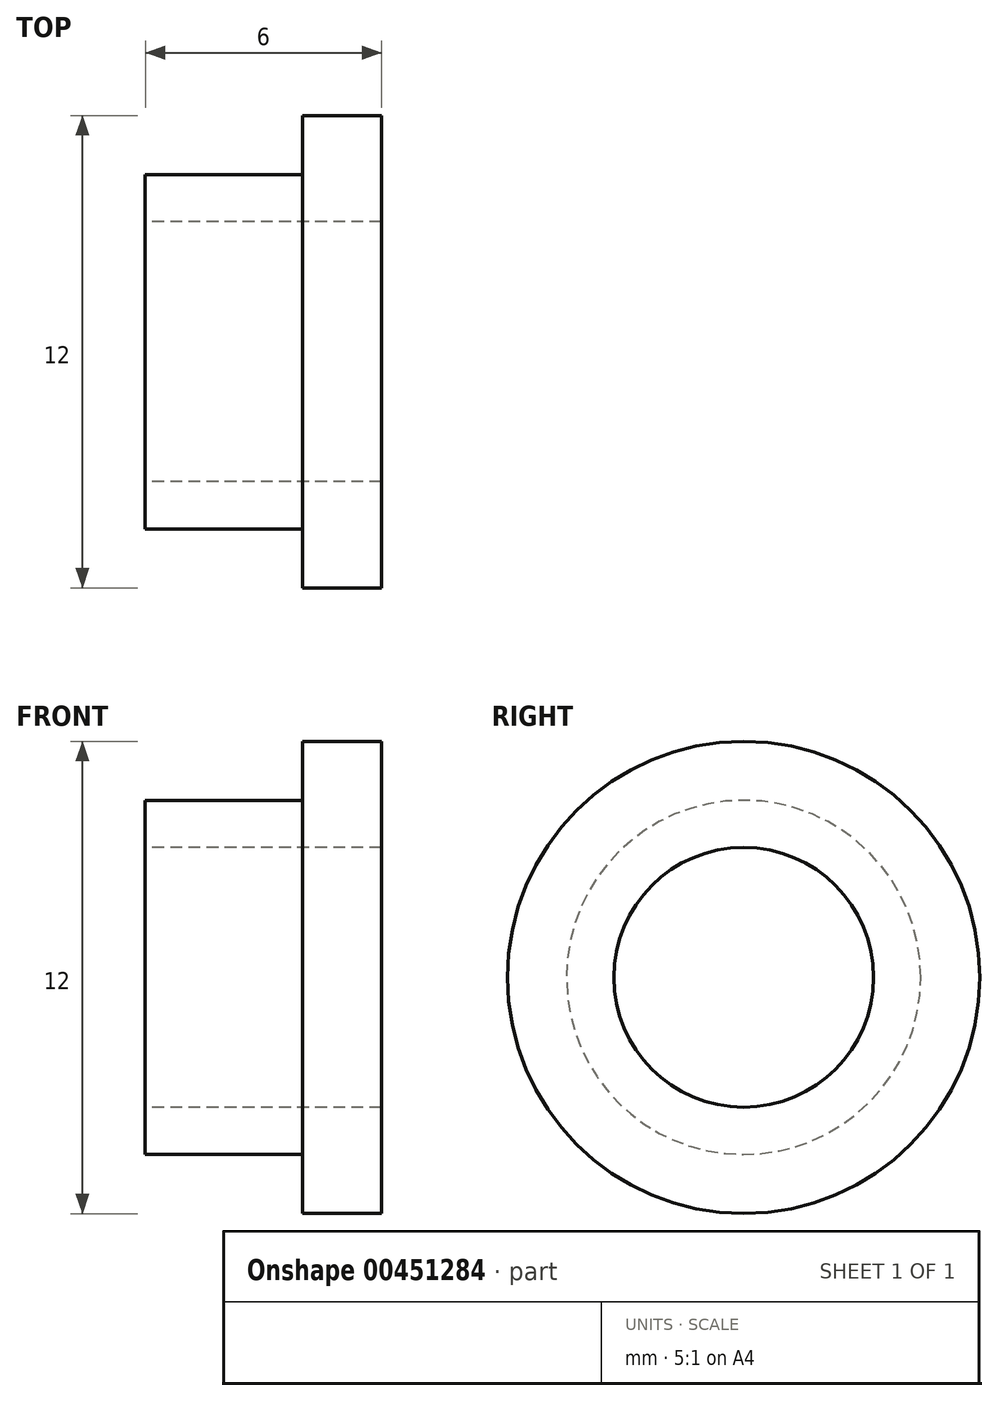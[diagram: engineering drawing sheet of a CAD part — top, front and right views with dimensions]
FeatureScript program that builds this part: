
annotation { "Feature Type Name" : "Feature", "Feature Type Description" : "" }
export const myFeature = defineFeature(function(context is Context, id is Id, definition is map)
    precondition{}
    {
        {
            var Q0;
            Q0=qCreatedBy(makeId("Front.planeOp"),FACE);
            var sketch = newSketch(context, id + "F0", { "sketchPlane" : qUnion([Q0])});
            skLineSegment(sketch, "E0", {"start": v(-81.68, -151.16) * mm, "end": v(-81.68, -149.66) * mm});
            skLineSegment(sketch, "E1", {"start": v(-79.68, -151.16) * mm, "end": v(-79.68, -139.16) * mm});
            skLineSegment(sketch, "E2", {"start": v(-85.68, -140.66) * mm, "end": v(-81.68, -140.66) * mm});
            skLineSegment(sketch, "E3", {"start": v(-85.68, -149.66) * mm, "end": v(-81.68, -149.66) * mm});
            skLineSegment(sketch, "E4", {"start": v(-85.68, -141.86) * mm, "end": v(-79.68, -141.86) * mm});
            skLineSegment(sketch, "E5", {"start": v(-85.68, -148.46) * mm, "end": v(-79.68, -148.46) * mm});
            skLineSegment(sketch, "E6", {"start": v(-87.9, -145.16) * mm, "end": v(-77.51, -145.16) * mm});
            skLineSegment(sketch, "E7", {"start": v(-81.68, -151.16) * mm, "end": v(-79.68, -151.16) * mm});
            skLineSegment(sketch, "E8", {"start": v(-81.68, -139.16) * mm, "end": v(-79.68, -139.16) * mm});
            skLineSegment(sketch, "E9", {"start": v(-85.68, -149.66) * mm, "end": v(-85.68, -140.66) * mm});
            skLineSegment(sketch, "E10", {"start": v(-81.68, -140.66) * mm, "end": v(-81.68, -139.16) * mm});
            skSolve(sketch);
        }
        {
            var Q0;
            {var subQ2=sQuery(id+"F0.wireOp",EDGE,"E2");Q0=makeQuery(id+"F0.imprint","IMPRINT",FACE,{"disambiguationData":[TD([[makeQuery(id+"F0.imprint","IMPRINT",EDGE,{"derivedFrom":subQ2}),-1.0]])]});}
            var Q1;
            Q1=sQuery(id+"F0.wireOp",EDGE,"E6");
            revolve(context, id + "F1", {"entities" : qUnion([Q0]), "axis" : qUnion([Q1]), "revolveType" : RevolveType.FULL});
        }
    });
